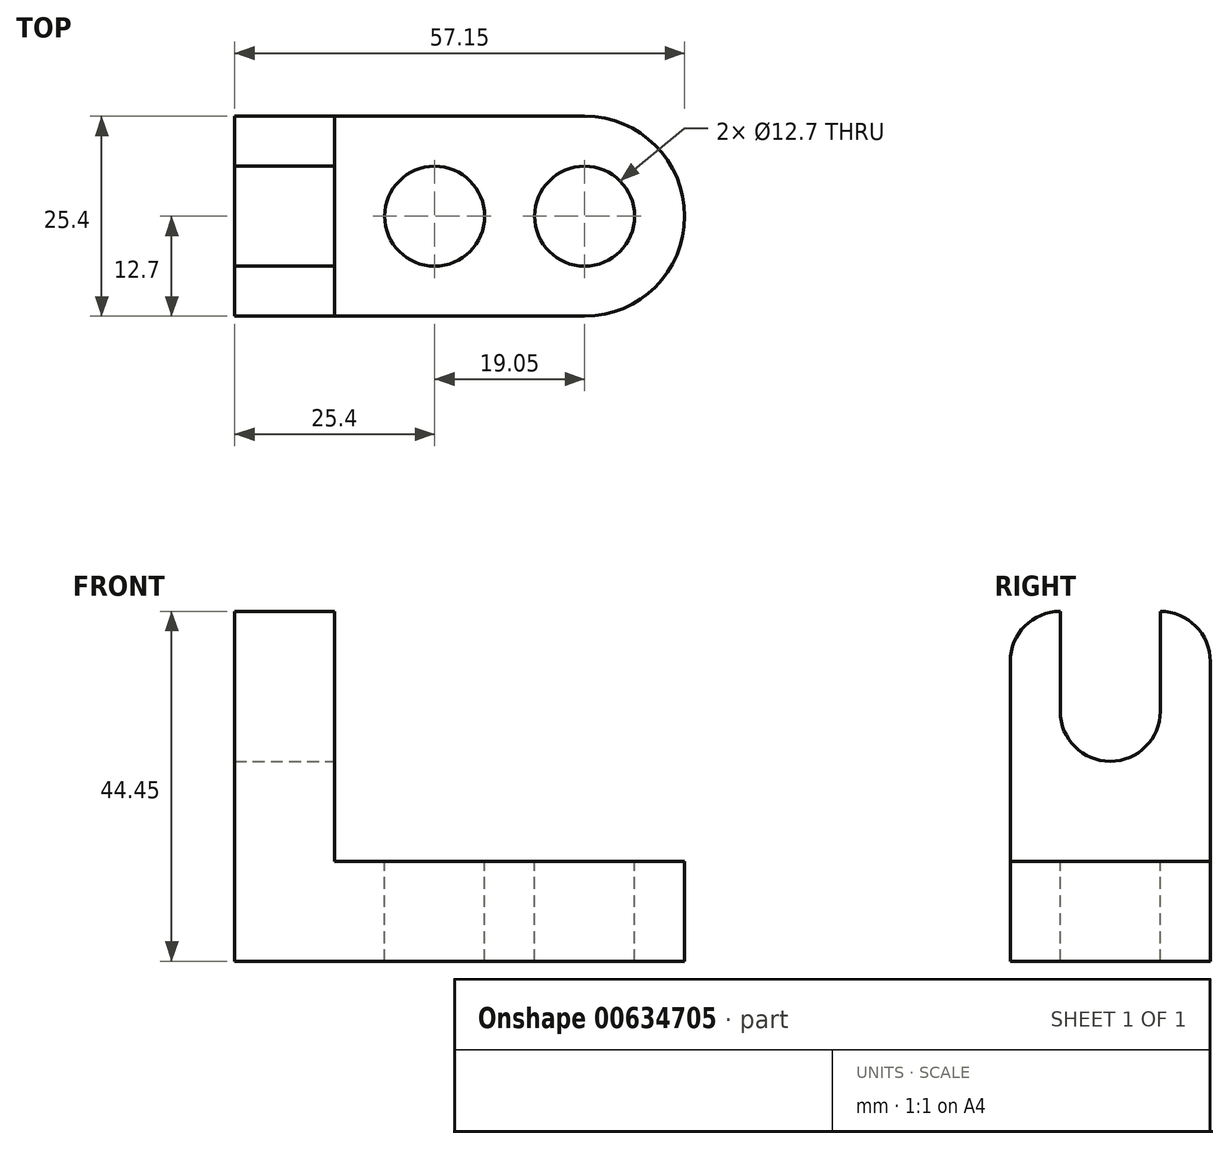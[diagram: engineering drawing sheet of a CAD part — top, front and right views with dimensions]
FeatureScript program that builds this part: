
annotation { "Feature Type Name" : "Feature", "Feature Type Description" : "" }
export const myFeature = defineFeature(function(context is Context, id is Id, definition is map)
    precondition{}
    {
        {
            var Q0;
            Q0=qCreatedBy(makeId("Front.planeOp"),FACE);
            var sketch = newSketch(context, id + "F0", { "sketchPlane" : qUnion([Q0])});
            skLineSegment(sketch, "E0", {"start": v(0, 0) * mm, "end": v(57.15, 0) * mm});
            skLineSegment(sketch, "E1", {"start": v(57.15, 0) * mm, "end": v(57.15, 12.7) * mm});
            skLineSegment(sketch, "E2", {"start": v(57.15, 12.7) * mm, "end": v(12.7, 12.7) * mm});
            skLineSegment(sketch, "E3", {"start": v(12.7, 12.7) * mm, "end": v(12.7, 44.45) * mm});
            skLineSegment(sketch, "E4", {"start": v(12.7, 44.45) * mm, "end": v(0, 44.45) * mm});
            skLineSegment(sketch, "E5", {"start": v(0, 44.45) * mm, "end": v(0, 0) * mm});
            skSolve(sketch);
        }
        {
            var Q0;
            Q0=qSketchRegion(id+"F0",true);
            extrude(context, id + "F1", {"entities" : qUnion([Q0]), "depth" : 25.4 * mm, "offsetDistance" : 25.4 * mm});
        }
        {
            var Q0;
            Q0=makeQuery(id+"F1.opExtrude","SWEPT_FACE",FACE,{"disambiguationData":[OSD([sQuery(id+"F0.wireOp",EDGE,"E2")])]});
            var sketch = newSketch(context, id + "F2", { "sketchPlane" : qUnion([Q0])});
            skCircle(sketch, "E6", {"center": v(25.4, -12.7) * mm, "radius": 6.35 * mm});
            skCircle(sketch, "E7", {"center": v(44.45, -12.7) * mm, "radius": 6.35 * mm});
            skArc(sketch, "E8", {"start": v(44.45, -25.4) * mm, "mid": v(57.15, -12.7) * mm, "end": v(44.45, 0) * mm});
            skSolve(sketch);
        }
        {
            var Q0;
            Q0=makeQuery(id+"F2.imprint","IMPRINT",FACE,{"disambiguationData":[TD([[makeQuery(id+"F2.imprint","IMPRINT",EDGE,{"derivedFrom":sQuery(id+"F2.wireOp",EDGE,"E6")}),1.0]])]});
            var Q1;
            Q1=makeQuery(id+"F2.imprint","IMPRINT",FACE,{"disambiguationData":[TD([[makeQuery(id+"F2.imprint","IMPRINT",EDGE,{"derivedFrom":sQuery(id+"F2.wireOp",EDGE,"E7")}),1.0]])]});
            var Q2;
            {var subQ0=sQuery(id+"F2.wireOp",EDGE,"E8");var subQ1=sQuery(id+"F0.wireOp",EDGE,"E2");var subQ2=makeQuery(id+"F1.opExtrude","CAP_EDGE",EDGE,{"disambiguationData":[OSD([subQ1])],"isStart":false});var subQ3=makeQuery(id+"F2.imprint","INTERSECT",VERTEX,{"derivedFrom":[subQ2,subQ0]});Q2=makeQuery(id+"F2.imprint","IMPRINT",FACE,{"disambiguationData":[TD([[makeQuery(id+"F2.imprint","IMPRINT",EDGE,{"disambiguationData":[TD([[subQ3,-1.0]])],"derivedFrom":subQ0}),-1.0]])]});}
            var Q3;
            {var subQ0=sQuery(id+"F2.wireOp",EDGE,"E8");var subQ1=sQuery(id+"F0.wireOp",EDGE,"E2");var subQ2=makeQuery(id+"F1.opExtrude","CAP_EDGE",EDGE,{"disambiguationData":[OSD([subQ1])],"isStart":true});var subQ3=makeQuery(id+"F2.imprint","INTERSECT",VERTEX,{"derivedFrom":[subQ2,subQ0]});Q3=makeQuery(id+"F2.imprint","IMPRINT",FACE,{"disambiguationData":[TD([[makeQuery(id+"F2.imprint","IMPRINT",EDGE,{"disambiguationData":[TD([[subQ3,1.0]])],"derivedFrom":subQ0}),-1.0]])]});}
            extrude(context, id + "F3", {"entities" : qUnion([Q0, Q1, Q2, Q3]), "operationType" : NewBodyOperationType.REMOVE, "oppositeDirection" : true, "depth" : 25.4 * mm, "offsetDistance" : 25.4 * mm});
        }
        {
            var Q0;
            Q0=makeQuery(id+"F1.opExtrude","SWEPT_FACE",FACE,{"disambiguationData":[OSD([sQuery(id+"F0.wireOp",EDGE,"E3")])]});
            var sketch = newSketch(context, id + "F4", { "sketchPlane" : qUnion([Q0])});
            skLineSegment(sketch, "E9", {"start": v(-19.05, 44.45) * mm, "end": v(-19.05, 31.75) * mm});
            skLineSegment(sketch, "E10", {"start": v(-6.35, 44.45) * mm, "end": v(-6.35, 31.75) * mm});
            skCircle(sketch, "E11", {"center": v(-12.7, 31.75) * mm, "radius": 6.35 * mm});
            skSolve(sketch);
        }
        {
            var Q0;
            Q0=qSketchRegion(id+"F4",true);
            var Q1;
            {var subQ0=sQuery(id+"F4.wireOp",EDGE,"E9");Q1=makeQuery(id+"F4.imprint","IMPRINT",FACE,{"disambiguationData":[TD([[makeQuery(id+"F4.imprint","IMPRINT",EDGE,{"derivedFrom":subQ0}),1.0]])]});}
            extrude(context, id + "F5", {"entities" : qUnion([Q0, Q1]), "operationType" : NewBodyOperationType.REMOVE, "oppositeDirection" : true, "depth" : 25.4 * mm, "offsetDistance" : 25.4 * mm});
        }
        {
            var Q0;
            Q0=makeQuery(id+"F1.opExtrude","SWEPT_FACE",FACE,{"disambiguationData":[OSD([sQuery(id+"F0.wireOp",EDGE,"E3")])]});
            var sketch = newSketch(context, id + "F6", { "sketchPlane" : qUnion([Q0])});
            skArc(sketch, "E12", {"start": v(-19.05, 44.45) * mm, "mid": v(-23.54, 42.6) * mm, "end": v(-25.4, 38.1) * mm});
            skPoint(sketch, "E12.endSnap0", {"position": v(-19.05, 38.1) * mm});
            skArc(sketch, "E13", {"start": v(0, 38.1) * mm, "mid": v(-1.86, 42.6) * mm, "end": v(-6.35, 44.45) * mm});
            skSolve(sketch);
        }
        {
            var Q0;
            {var subQ0=sQuery(id+"F6.wireOp",EDGE,"E12");Q0=makeQuery(id+"F6.imprint","IMPRINT",FACE,{"disambiguationData":[TD([[makeQuery(id+"F6.imprint","IMPRINT",EDGE,{"derivedFrom":subQ0}),-1.0]])]});}
            var Q1;
            {var subQ0=sQuery(id+"F6.wireOp",EDGE,"E13");Q1=makeQuery(id+"F6.imprint","IMPRINT",FACE,{"disambiguationData":[TD([[makeQuery(id+"F6.imprint","IMPRINT",EDGE,{"derivedFrom":subQ0}),-1.0]])]});}
            extrude(context, id + "F7", {"entities" : qUnion([Q0, Q1]), "operationType" : NewBodyOperationType.REMOVE, "oppositeDirection" : true, "depth" : 25.4 * mm, "offsetDistance" : 25.4 * mm});
        }
    });
